# Revit family: Assa-Abloy_ Revolving_UniTurn
name_source: partatom
category: Doors
units: mm (PartAtom-declared; Revit-internal decimal feet)

## family parameters
Always vertical = Yes
Cut with Voids When Loaded = No
Host = Wall
OmniClass Number = 23.30.10.00
OmniClass Title = Doors
Room Calculation Point = No
Shared = No

## types (4) — shared parameters
Analytic Construction = <None>
BIMobject category = Doors
Construction Type = Automatic Revolving Door
Date of publishing = 3/28/2014
Depth (mm) = 0' - 0"
Design country = Sweden
Disclaimer = Consult product specification for sensors to comply with ANSI A156.27.
Distance = 0' - 6 11/16"
Edition number = 1
Frame angle = 31.25°
Function = Exterior
Height (mm) = 0' - 0"
IFC Classification = Door
Manufacturer = ASSA ABLOY Entrance Systems
Manufacturer country = Czech Republic
Material main = Aluminium
Material secondary = Glass
Model = UniTurn
NBS Reference Code = 25-30-20-70
NBS Reference Description = Revolving Doorset Systems
Name of the object = UniTurn
Product SKU = UNI
Product family = Automatic Revolving Doors
Product group = Besam Large 2-wing UniTurn
Product name = Besam Revolving Doors UniTurn
UNSPSC Code = 301715
URL = www.assaabloyentrance.us
Uniclass 1.4 Code = L411
Uniclass 1.4 Description = Doors
Uniclass 2.0 Code = SS-25-30-20-70
Uniclass 2.0 Description = Revolving Doorset Systems
Wall Closure = By host
Weight Net (Kg) = 0
Width (mm) = 0' - 0"

## per-type parameters (varying)
| type | Distance 1 | Manufacturer URL | Manufacturer name | Radius 1 | Radius 2 | Radius 3 | Radius 4 | TW | Width |
| UniTurn 12' | 5' - 10 21/32" | www.assaabloyentrance.us | Besam | 5' - 10 23/32" | 6' - 0 13/32" | 6' - 0 9/32" | 6' - 0 11/32" | 5' - 10 7/8" | 12' - 0 7/8" |
| UniTurn 14' | 6' - 10 15/32" | www.assaabloyentrance.us | ASSA ABLOY Entrance Systems | 6' - 10 17/32" | 7' - 0 7/32" | 7' - 0 3/32" | 7' - 0 5/32" | 6' - 10 11/16" | 14' - 0 1/2" |
| UniTurn 16' | 7' - 10 9/32" |  | ASSA ABLOY Entrance Systems | 7' - 10 11/32" | 8' - 0 1/32" | 7' - 11 29/32" | 7' - 11 31/32" | 7' - 10 1/2" | 16' - 0 1/8" |
| UniTurn 18' | 8' - 10 3/32" |  | Besam | 8' - 10 5/32" | 8' - 11 27/32" | 8' - 11 23/32" | 8' - 11 25/32" | 8' - 10 1/4" | 17' - 11 3/4" |

## geometry (parser evidence)
native form markers: Blend x4, Sweep x4
no freeform markers — native parametric forms only
